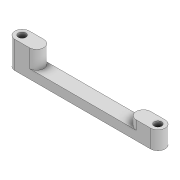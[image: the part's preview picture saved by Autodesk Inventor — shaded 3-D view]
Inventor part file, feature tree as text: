
AUTODESK INVENTOR PART (.ipt)
format: ipt  version: 2022 (Build 260153000, 153)  size: 116,736 bytes
history: native  units: mm
features: extrude x3, sketch x2, projected_geometry x1
ambient origin geometry x8: Origin, YZ Plane, XZ Plane, XY Plane, X Axis, Y Axis, Z Axis, Center Point
bodies: Solid1 (feature_tree)
feature tree (6):
  extrude  "Extrusion1"  Depth=8.0mm
  sketch  "Sketch4"  dims[d2=4.2mm d4=5.0mm d5=0.0mm d10=4.2mm d30=8.0mm d31=8.0mm d32=8.0mm d33=8.0mm d34=10.0mm d35=0.0mm d36=5.0mm d37=0.0mm]
  extrude  "Extrusion7"  Depth=5.0mm TaperAngle=0.0deg
  extrude  "Extrusion8"  Depth=5.0mm
  sketch  "Sketch1"  dims[d0=75.105mm d1=8.0mm]
  projected_geometry  "Projected Loop3"
